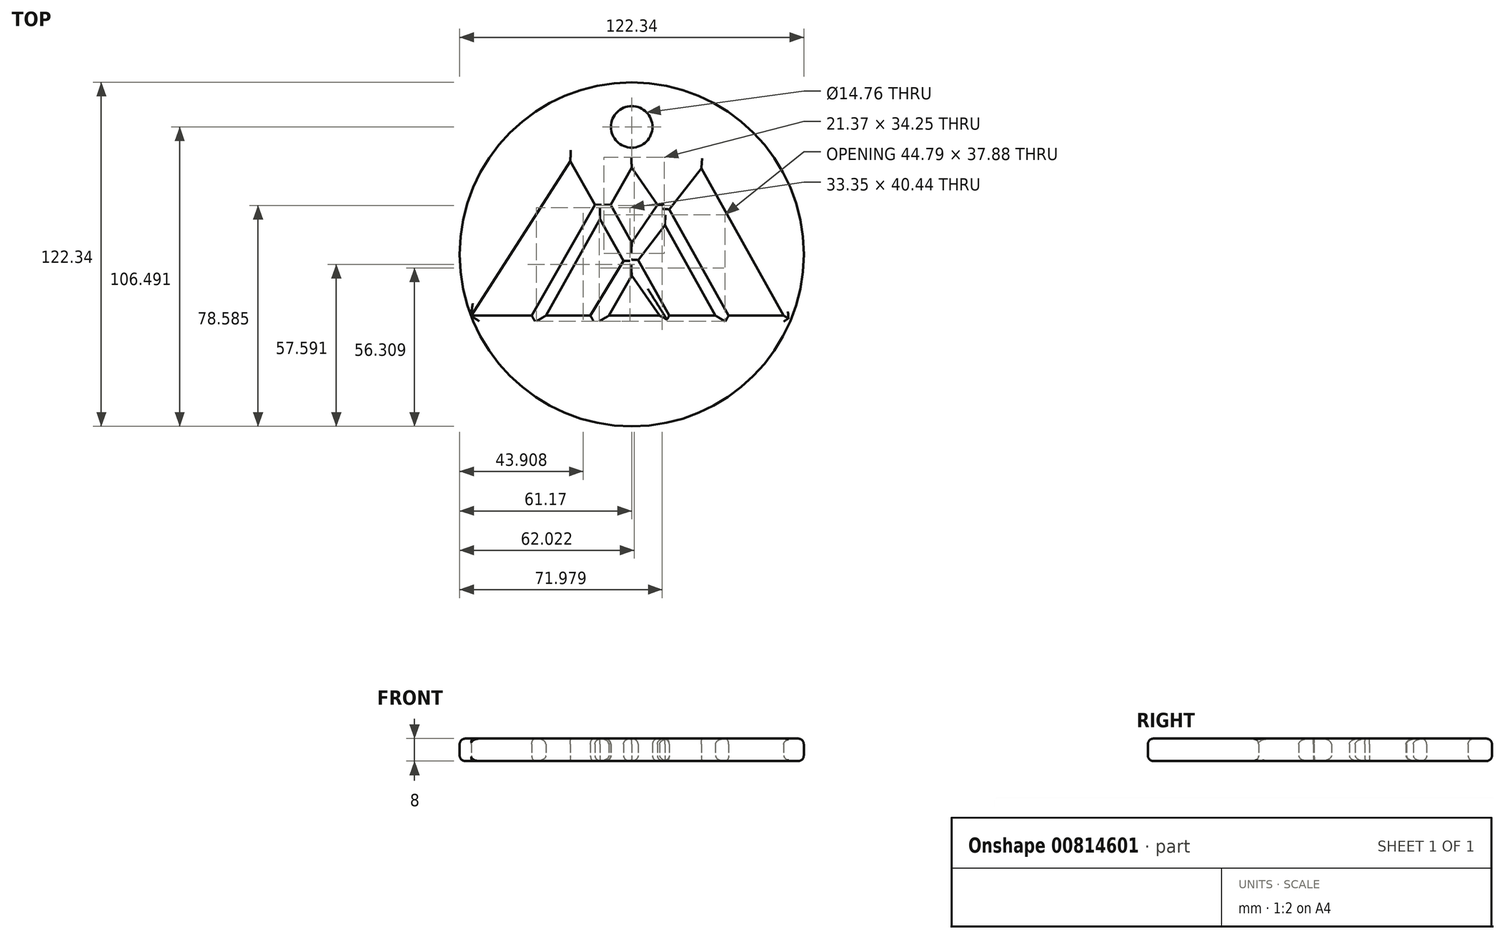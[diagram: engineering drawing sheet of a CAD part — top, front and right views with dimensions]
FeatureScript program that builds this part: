
annotation { "Feature Type Name" : "Feature", "Feature Type Description" : "" }
export const myFeature = defineFeature(function(context is Context, id is Id, definition is map)
    precondition{}
    {
        {
            var Q0;
            Q0=qCreatedBy(makeId("Top.planeOp"),FACE);
            var sketch = newSketch(context, id + "F0", { "sketchPlane" : qUnion([Q0])});
            skLineSegment(sketch, "E0", {"start": v(-21.8, 33.16) * mm, "end": v(-13.08, 17.57) * mm});
            skLineSegment(sketch, "E1", {"start": v(-13.08, 17.57) * mm, "end": v(-35.54, -21.8) * mm});
            skLineSegment(sketch, "E2", {"start": v(-35.54, -21.8) * mm, "end": v(-56.95, -21.8) * mm});
            skLineSegment(sketch, "E3", {"start": v(-56.95, -21.8) * mm, "end": v(-21.8, 33.16) * mm});
            skLineSegment(sketch, "E4", {"start": v(-11.23, 12.55) * mm, "end": v(-2.9, -2.35) * mm});
            skLineSegment(sketch, "E5", {"start": v(-2.9, -2.35) * mm, "end": v(-14.67, -21.8) * mm});
            skLineSegment(sketch, "E6", {"start": v(-14.67, -21.8) * mm, "end": v(-30.52, -21.8) * mm});
            skLineSegment(sketch, "E7", {"start": v(-30.52, -21.8) * mm, "end": v(-11.23, 12.55) * mm});
            skLineSegment(sketch, "E8", {"start": v(11.76, 10.44) * mm, "end": v(29.8, -21.8) * mm});
            skLineSegment(sketch, "E9", {"start": v(29.8, -21.8) * mm, "end": v(13.35, -21.8) * mm});
            skLineSegment(sketch, "E10", {"start": v(13.35, -21.8) * mm, "end": v(2.28, -2.02) * mm});
            skLineSegment(sketch, "E11", {"start": v(2.28, -2.02) * mm, "end": v(11.76, 10.44) * mm});
            skLineSegment(sketch, "E12", {"start": v(13.35, 15.99) * mm, "end": v(34.48, -21.8) * mm});
            skLineSegment(sketch, "E13", {"start": v(34.48, -21.8) * mm, "end": v(54.04, -21.8) * mm});
            skLineSegment(sketch, "E14", {"start": v(54.04, -21.8) * mm, "end": v(24.76, 30.55) * mm});
            skLineSegment(sketch, "E15", {"start": v(24.76, 30.55) * mm, "end": v(13.35, 15.99) * mm});
            skLineSegment(sketch, "E16", {"start": v(0, 30.79) * mm, "end": v(-7.54, 17.57) * mm});
            skLineSegment(sketch, "E17", {"start": v(-7.54, 17.57) * mm, "end": v(0, 4.1) * mm});
            skLineSegment(sketch, "E18", {"start": v(0, -7.53) * mm, "end": v(-8.14, -21.8) * mm});
            skLineSegment(sketch, "E19", {"start": v(-8.14, -21.8) * mm, "end": v(9.9, -21.8) * mm});
            skLineSegment(sketch, "E20", {"start": v(9.9, -21.8) * mm, "end": v(0, -7.53) * mm});
            skLineSegment(sketch, "E21", {"start": v(0, 30.79) * mm, "end": v(9.12, 17.57) * mm});
            skLineSegment(sketch, "E22", {"start": v(9.12, 17.57) * mm, "end": v(0, 4.1) * mm});
            skCircle(sketch, "E23", {"center": v(0, 0) * mm, "radius": 61.17 * mm});
            skCircle(sketch, "E24", {"center": v(0, 45.32) * mm, "radius": 7.38 * mm});
            skSolve(sketch);
        }
        {
            var Q0;
            Q0 = qSketchRegion(id + "F0", true);
            extrude(context, id + "F1", {"entities" : qUnion([Q0]), "depth" : 8 * mm, "offsetDistance" : 25 * mm});
        }
        {
            var Q0;
            Q0=makeQuery(id+"F1.opExtrude","CAP_EDGE",EDGE,{"disambiguationData":[OSD([sQuery(id+"F0.wireOp",EDGE,"E0")])],"isStart":false});
            var Q1;
            Q1=makeQuery(id+"F1.opExtrude","CAP_EDGE",EDGE,{"disambiguationData":[OSD([sQuery(id+"F0.wireOp",EDGE,"E1")])],"isStart":false});
            var Q2;
            Q2=makeQuery(id+"F1.opExtrude","CAP_EDGE",EDGE,{"disambiguationData":[OSD([sQuery(id+"F0.wireOp",EDGE,"E3")])],"isStart":false});
            var Q3;
            Q3=makeQuery(id+"F1.opExtrude","CAP_EDGE",EDGE,{"disambiguationData":[OSD([sQuery(id+"F0.wireOp",EDGE,"E2")])],"isStart":false});
            var Q4;
            Q4=makeQuery(id+"F1.opExtrude","CAP_EDGE",EDGE,{"disambiguationData":[OSD([sQuery(id+"F0.wireOp",EDGE,"E4")])],"isStart":false});
            var Q5;
            Q5=makeQuery(id+"F1.opExtrude","CAP_EDGE",EDGE,{"disambiguationData":[OSD([sQuery(id+"F0.wireOp",EDGE,"E5")])],"isStart":false});
            var Q6;
            Q6=makeQuery(id+"F1.opExtrude","CAP_EDGE",EDGE,{"disambiguationData":[OSD([sQuery(id+"F0.wireOp",EDGE,"E6")])],"isStart":false});
            var Q7;
            Q7=makeQuery(id+"F1.opExtrude","CAP_EDGE",EDGE,{"disambiguationData":[OSD([sQuery(id+"F0.wireOp",EDGE,"E7")])],"isStart":false});
            var Q8;
            Q8=makeQuery(id+"F1.opExtrude","CAP_EDGE",EDGE,{"disambiguationData":[OSD([sQuery(id+"F0.wireOp",EDGE,"E18")])],"isStart":false});
            var Q9;
            Q9=makeQuery(id+"F1.opExtrude","CAP_EDGE",EDGE,{"disambiguationData":[OSD([sQuery(id+"F0.wireOp",EDGE,"E20")])],"isStart":false});
            var Q10;
            Q10=makeQuery(id+"F1.opExtrude","CAP_EDGE",EDGE,{"disambiguationData":[OSD([sQuery(id+"F0.wireOp",EDGE,"E19")])],"isStart":false});
            var Q11;
            Q11=makeQuery(id+"F1.opExtrude","CAP_EDGE",EDGE,{"disambiguationData":[OSD([sQuery(id+"F0.wireOp",EDGE,"E10")])],"isStart":false});
            var Q12;
            Q12=makeQuery(id+"F1.opExtrude","CAP_EDGE",EDGE,{"disambiguationData":[OSD([sQuery(id+"F0.wireOp",EDGE,"E8")])],"isStart":false});
            var Q13;
            Q13=makeQuery(id+"F1.opExtrude","CAP_EDGE",EDGE,{"disambiguationData":[OSD([sQuery(id+"F0.wireOp",EDGE,"E9")])],"isStart":false});
            var Q14;
            Q14=makeQuery(id+"F1.opExtrude","CAP_EDGE",EDGE,{"disambiguationData":[OSD([sQuery(id+"F0.wireOp",EDGE,"E11")])],"isStart":false});
            var Q15;
            Q15=makeQuery(id+"F1.opExtrude","CAP_EDGE",EDGE,{"disambiguationData":[OSD([sQuery(id+"F0.wireOp",EDGE,"E12")])],"isStart":false});
            var Q16;
            Q16=makeQuery(id+"F1.opExtrude","CAP_EDGE",EDGE,{"disambiguationData":[OSD([sQuery(id+"F0.wireOp",EDGE,"E15")])],"isStart":false});
            var Q17;
            Q17=makeQuery(id+"F1.opExtrude","CAP_EDGE",EDGE,{"disambiguationData":[OSD([sQuery(id+"F0.wireOp",EDGE,"E14")])],"isStart":false});
            var Q18;
            Q18=makeQuery(id+"F1.opExtrude","CAP_EDGE",EDGE,{"disambiguationData":[OSD([sQuery(id+"F0.wireOp",EDGE,"E13")])],"isStart":false});
            var Q19;
            Q19=makeQuery(id+"F1.opExtrude","CAP_EDGE",EDGE,{"disambiguationData":[OSD([sQuery(id+"F0.wireOp",EDGE,"E21")])],"isStart":false});
            var Q20;
            Q20=makeQuery(id+"F1.opExtrude","CAP_EDGE",EDGE,{"disambiguationData":[OSD([sQuery(id+"F0.wireOp",EDGE,"E16")])],"isStart":false});
            var Q21;
            Q21=makeQuery(id+"F1.opExtrude","CAP_EDGE",EDGE,{"disambiguationData":[OSD([sQuery(id+"F0.wireOp",EDGE,"E17")])],"isStart":false});
            var Q22;
            Q22=makeQuery(id+"F1.opExtrude","CAP_EDGE",EDGE,{"disambiguationData":[OSD([sQuery(id+"F0.wireOp",EDGE,"E22")])],"isStart":false});
            var Q23;
            Q23=makeQuery(id+"F1.opExtrude","CAP_EDGE",EDGE,{"disambiguationData":[OSD([sQuery(id+"F0.wireOp",EDGE,"E24")])],"isStart":false});
            var Q24;
            Q24=makeQuery(id+"F1.opExtrude","CAP_FACE",FACE,{"disambiguationData":[OSD([sQuery(id+"F0.wireOp",EDGE,"E0"),sQuery(id+"F0.wireOp",EDGE,"E1"),sQuery(id+"F0.wireOp",EDGE,"E2"),sQuery(id+"F0.wireOp",EDGE,"E3"),sQuery(id+"F0.wireOp",EDGE,"E4"),sQuery(id+"F0.wireOp",EDGE,"E5"),sQuery(id+"F0.wireOp",EDGE,"E6"),sQuery(id+"F0.wireOp",EDGE,"E7"),sQuery(id+"F0.wireOp",EDGE,"E8"),sQuery(id+"F0.wireOp",EDGE,"E9"),sQuery(id+"F0.wireOp",EDGE,"E10"),sQuery(id+"F0.wireOp",EDGE,"E11"),sQuery(id+"F0.wireOp",EDGE,"E12"),sQuery(id+"F0.wireOp",EDGE,"E13"),sQuery(id+"F0.wireOp",EDGE,"E14"),sQuery(id+"F0.wireOp",EDGE,"E15"),sQuery(id+"F0.wireOp",EDGE,"E16"),sQuery(id+"F0.wireOp",EDGE,"E17"),sQuery(id+"F0.wireOp",EDGE,"E18"),sQuery(id+"F0.wireOp",EDGE,"E19"),sQuery(id+"F0.wireOp",EDGE,"E20"),sQuery(id+"F0.wireOp",EDGE,"E21"),sQuery(id+"F0.wireOp",EDGE,"E22"),sQuery(id+"F0.wireOp",EDGE,"E23"),sQuery(id+"F0.wireOp",EDGE,"E24")])],"isStart":false});
            var Q25;
            Q25=makeQuery(id+"F1.opExtrude","CAP_FACE",FACE,{"disambiguationData":[OSD([sQuery(id+"F0.wireOp",EDGE,"E0"),sQuery(id+"F0.wireOp",EDGE,"E1"),sQuery(id+"F0.wireOp",EDGE,"E2"),sQuery(id+"F0.wireOp",EDGE,"E3"),sQuery(id+"F0.wireOp",EDGE,"E4"),sQuery(id+"F0.wireOp",EDGE,"E5"),sQuery(id+"F0.wireOp",EDGE,"E6"),sQuery(id+"F0.wireOp",EDGE,"E7"),sQuery(id+"F0.wireOp",EDGE,"E8"),sQuery(id+"F0.wireOp",EDGE,"E9"),sQuery(id+"F0.wireOp",EDGE,"E10"),sQuery(id+"F0.wireOp",EDGE,"E11"),sQuery(id+"F0.wireOp",EDGE,"E12"),sQuery(id+"F0.wireOp",EDGE,"E13"),sQuery(id+"F0.wireOp",EDGE,"E14"),sQuery(id+"F0.wireOp",EDGE,"E15"),sQuery(id+"F0.wireOp",EDGE,"E16"),sQuery(id+"F0.wireOp",EDGE,"E17"),sQuery(id+"F0.wireOp",EDGE,"E18"),sQuery(id+"F0.wireOp",EDGE,"E19"),sQuery(id+"F0.wireOp",EDGE,"E20"),sQuery(id+"F0.wireOp",EDGE,"E21"),sQuery(id+"F0.wireOp",EDGE,"E22"),sQuery(id+"F0.wireOp",EDGE,"E23"),sQuery(id+"F0.wireOp",EDGE,"E24")])],"isStart":true});
            fillet(context, id + "F2", {"entities" : qUnion([Q0, Q1, Q2, Q3, Q4, Q5, Q6, Q7, Q8, Q9, Q10, Q11, Q12, Q13, Q14, Q15, Q16, Q17, Q18, Q19, Q20, Q21, Q22, Q23, Q24, Q25]), "radius" : 2 * mm, "tangentPropagation" : true, "allowEdgeOverflow" : false});
        }
    });
